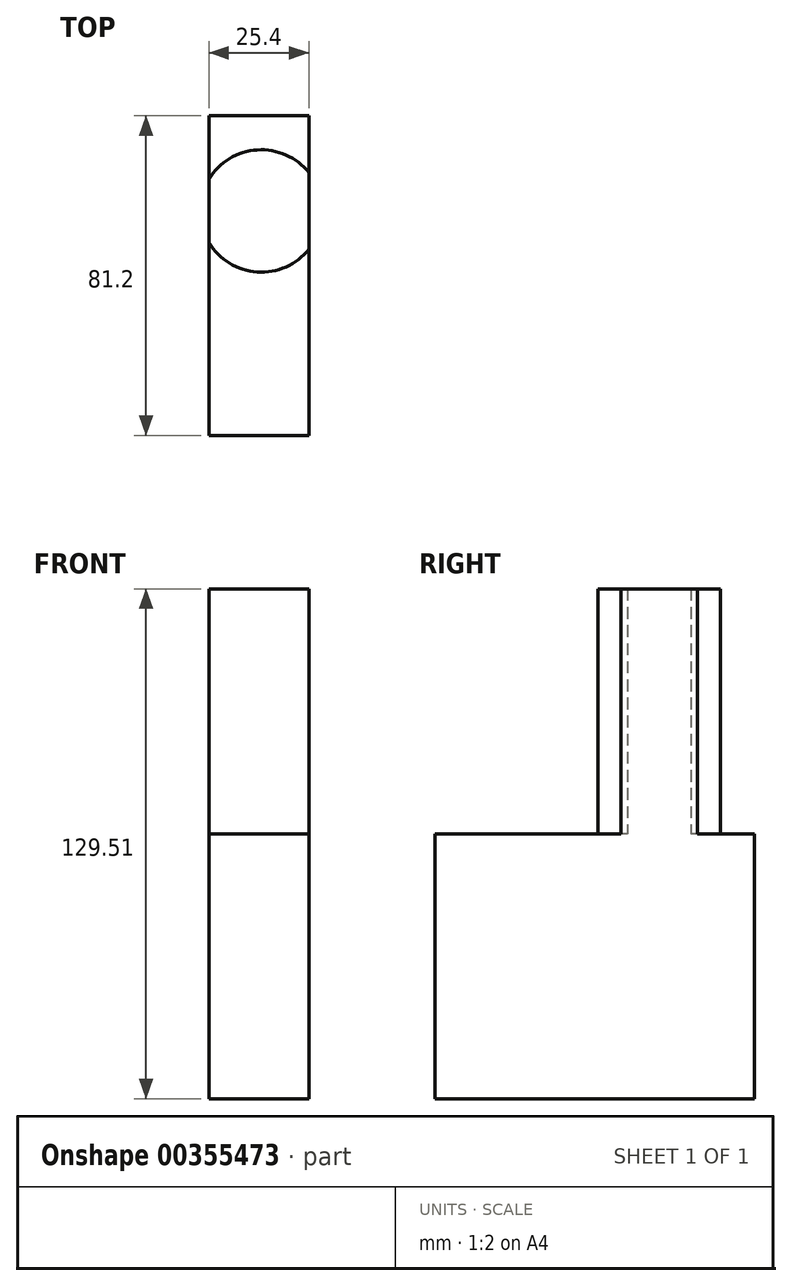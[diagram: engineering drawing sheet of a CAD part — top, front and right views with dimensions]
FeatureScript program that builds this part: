
annotation { "Feature Type Name" : "Feature", "Feature Type Description" : "" }
export const myFeature = defineFeature(function(context is Context, id is Id, definition is map)
    precondition{}
    {
        {
            var Q0;
            Q0=qCreatedBy(makeId("Right.planeOp"),FACE);
            var sketch = newSketch(context, id + "F0", { "sketchPlane" : qUnion([Q0])});
            skLineSegment(sketch, "E0.bottom", {"start": v(48.82, 41.7) * mm, "end": v(-32.38, 41.7) * mm});
            skLineSegment(sketch, "E0.top", {"start": v(48.82, -25.54) * mm, "end": v(-32.38, -25.54) * mm});
            skLineSegment(sketch, "E0.left", {"start": v(48.82, 41.7) * mm, "end": v(48.82, -25.54) * mm});
            skLineSegment(sketch, "E0.right", {"start": v(-32.38, 41.7) * mm, "end": v(-32.38, -25.54) * mm});
            skSolve(sketch);
        }
        {
            var Q0;
            Q0=makeQuery(id+"F0.imprint","IMPRINT",FACE,{"disambiguationData":[TD([[makeQuery(id+"F0.imprint","IMPRINT",EDGE,{"derivedFrom":sQuery(id+"F0.wireOp",EDGE,"E0.bottom")}),1.0]])]});
            extrude(context, id + "F1", {"entities" : qUnion([Q0]), "depth" : 25.4 * mm});
        }
        {
            var Q0;
            Q0=makeQuery(id+"F1.opExtrude","SWEPT_FACE",FACE,{"disambiguationData":[OSD([sQuery(id+"F0.wireOp",EDGE,"E0.bottom")])]});
            var sketch = newSketch(context, id + "F2", { "sketchPlane" : qUnion([Q0])});
            skCircle(sketch, "E1", {"center": v(13.28, 24.65) * mm, "radius": 15.54 * mm});
            skSolve(sketch);
        }
        {
            var Q0;
            {var subQ0=sQuery(id+"F2.wireOp",EDGE,"E1");var subQ1=sQuery(id+"F0.wireOp",EDGE,"E0.bottom");var subQ2=makeQuery(id+"F1.opExtrude","CAP_EDGE",EDGE,{"disambiguationData":[OSD([subQ1])],"isStart":true});var subQ3=makeQuery(id+"F2.imprint","INTERSECT",VERTEX,{"disambiguationData":[OD(0.0)],"derivedFrom":[subQ2,subQ0]});Q0=makeQuery(id+"F2.imprint","IMPRINT",FACE,{"disambiguationData":[TD([[makeQuery(id+"F2.imprint","IMPRINT",EDGE,{"disambiguationData":[TD([[subQ3,1.0]])],"derivedFrom":subQ0}),1.0]])]});}
            extrude(context, id + "F3", {"entities" : qUnion([Q0]), "operationType" : NewBodyOperationType.ADD, "depth" : 62.28 * mm});
        }
    });
